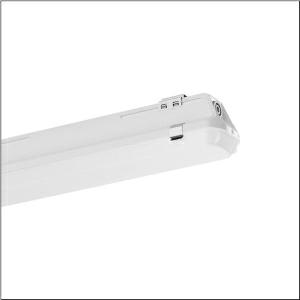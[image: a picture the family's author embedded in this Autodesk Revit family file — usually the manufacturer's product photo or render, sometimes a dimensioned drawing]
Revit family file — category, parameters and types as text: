
# Revit family: monsun_r__11_emergency_51fp20dp460hr_5229
name_source: partatom
category: Lighting Fixtures
units: mm (PartAtom-declared; Revit-internal decimal feet)

## family parameters
Cut with Voids When Loaded = No
Host = Face
Light Source = No
Part Type = Normal
Room Calculation Point = No
Round Connector Dimension = Use Diameter
Shared = No

## types (1)
- --- (1 x LED, 800 lm, 6.9 W, 4000K)
    Apparent Load = 7 VA
    CIE Flux Codes = 45 75 93 94 100
    Color Rendering = 80
    Color Temperature = 4000K
    Default Elevation = 1800 mm
    Description = Monsun® 11 emergency, damp-proof luminaire, chain hanger, primary optical cover: enclosure, of PC, light emission: direct distribution, primary light characteristic: symmetric, installation type: suspended mounting, surface-mounted, horizontal mounting, vertical mounting, LED, rated luminous flux: 5.450lm, luminous efficacy: 158lm/W, light colour: 840, colour temperature: 4000K, control gear: ECG DALI, with terminal, 5+2-pole, max. 2.5mm², mains connection: 220..240V, AC/DC, 0/50..60Hz, rated input power: 35W, changeover relay for equivalent power supply, AC/DC, 0/50..60Hz, luminaire housing, of glass-fibre reinforced polyester, uncoated, bright grey, incl. chain hanger, length: 1.590mm, width: 90mm, height: 88mm, clip for enclosure, of stainless steel (V2A), ceiling mounting element, of stainless steel (V2A), chain hanger, of stainless steel (V2A), protection rating (complete): IP66, insulation class (complete): insulation class I (protective earthing), certification: CE, UKCA, protection symbol: D, impact resistance: IK08, permissible operating ambient temperature: -25..+35°C, standard: EN 50419, EN 60598-2-1, EN 60598-2-22, no direct snow, no direct sun, no direct rain, for indoor or canopied outdoor use, corresponds to IFS (International Featured Standards) requirements for safety and quality in the food industry, contact your sales advisor before using the luminaires in applications with unclear chemical exposure, large temperature fluctuations or condensation-forming humidity, LABS conformity tested according to VDMA 24364:2018-05, packaging unit: 1 piece
    Height = 89 mm
    Lamp = 1 x LED
    Lamp Light Flux = 800 lm
    Lamp Power = 6.9 W
    Lamp count = 1
    Length = 1590 mm
    Luminous efficacy = 116 lm/W
    Manufacturer = Siteco
    ModVariant = No
    Model = 51FP20DP460HR
    Mounting Place = Ceiling
    Mounting Type = Surface mounted
    Number of Poles = 1
    OnlyDefault = Yes
    Power Factor = 1
    Product Name = Monsun® 11 emergency
    Product group = damp-proof luminaire
    ProductGroupID = 301
    Protection Class = Protection class I
    Protection Degree = IP 66
    RLX_Detail_Level = 1
    RLX_Emergency_Light_Flux = 0 lm
    RLX_Emergency_Type = 0
    RLX_Emergency_Type_DB = No
    RlxData = <blob elided: 92717 chars, md5=6acd77fc>
    Socket = socket
    Standby Power = 0 W
    System Light Flux = 800 lm
    System Power = 7 W
    Type Comments = : equivalent power supply (DC)
    Type Image = l_1004748.jpg
    URL = http://relux.com
    VarID = @adj_152525
    Voltage = 0 V
    Weight = 0.00 kg
    Width = 90 mm

## geometry (parser evidence)
native form markers: Blend x4, Sweep x14
no freeform markers — native parametric forms only
